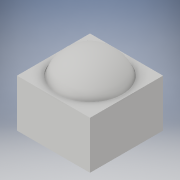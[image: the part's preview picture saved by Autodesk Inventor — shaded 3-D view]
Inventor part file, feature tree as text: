
AUTODESK INVENTOR PART (.ipt)
format: ipt  version: 2017 (Build 210142000, 142)  size: 191,488 bytes
history: native  units: in
note: dims shown in document units (in); Inventor stores cm internally (conversion verified against a paired STEP export)
features: other x4, sketch x2, extrude x1
ambient origin geometry x8: Origin, YZ Plane, XZ Plane, XY Plane, X Axis, Y Axis, Z Axis, Center Point
bodies: Body1 (feature_tree), Body2 (feature_tree)
feature tree (7):
  other  "cube for ball"
  sketch  "Sketch1"  dims[d0=3.069in d1=0.136in]
  extrude  "cube to cut from"  Depth=0.136in
  other  "cut out for mouse ball"
  other  "mouse ball"
  sketch  "Sketch2"  dims[d3=1.8065in d4=1.8065in d5=1.1239in d8=3.613in d9=0.0in d10=0.136in d11=0.02in d17=3.381in d18=180.0deg d19=3.613in d20=180.0deg d25=1.116in]
  other  "ball"
